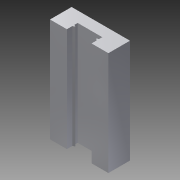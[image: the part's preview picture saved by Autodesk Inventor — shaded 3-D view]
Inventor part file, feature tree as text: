
AUTODESK INVENTOR PART (.ipt)
format: ipt  version: 2015 (Build 190159000, 159)  size: 111,104 bytes
history: native  units: mm
features: sketch x2, extrude x1, hole x1
ambient origin geometry x8: Origin, YZ Plane, XZ Plane, XY Plane, X Axis, Y Axis, Z Axis, Center Point
bodies: Solid1 (feature_tree)
feature tree (4):
  extrude  "Extrusion1"  Depth=10.0mm
  hole  "Hole1"  [1 undecoded]
  sketch  "Sketch1"  dims[d0=27.0mm d1=10.0mm]
  sketch  "Sketch2"  dims[d2=5.0mm d3=9.5mm d4=7.0mm d5=5.0mm d6=48.0mm d7=0.0mm d8=20.0mm d9=20.0mm d10=2.459mm d11=6.0mm d12=4.0mm d13=2.0mm d14=90.0deg d15=3.5mm d16=20.594885mm]
note: 1 required parameter value undecoded (feature->parameter linkage not recoverable at this tier; creation-order binding heuristic only, values carry confidence <= 0.55)
